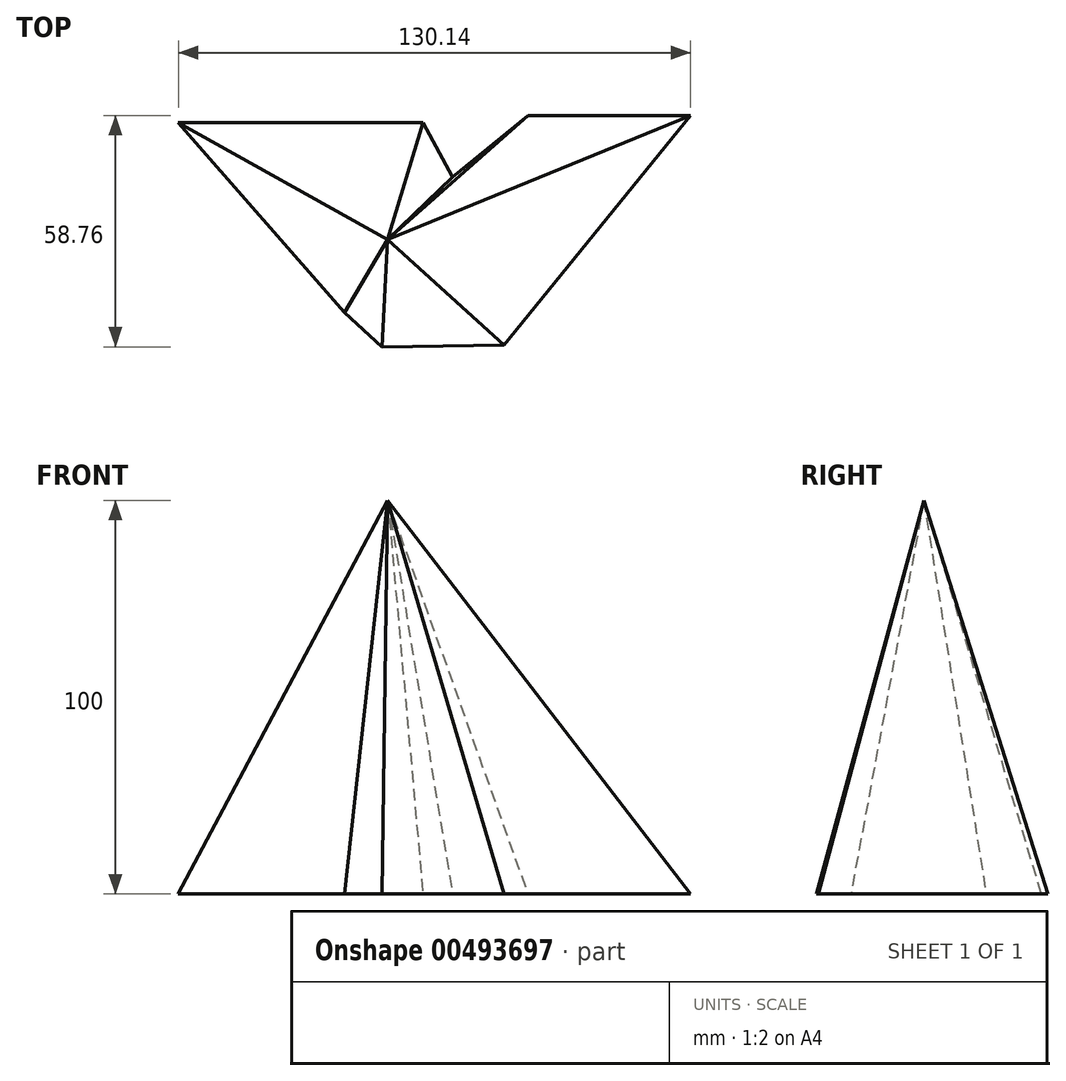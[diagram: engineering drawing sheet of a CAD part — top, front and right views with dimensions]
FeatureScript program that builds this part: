
annotation { "Feature Type Name" : "Feature", "Feature Type Description" : "" }
export const myFeature = defineFeature(function(context is Context, id is Id, definition is map)
    precondition{}
    {
        {
            var Q0;
            Q0=qCreatedBy(makeId("Top.planeOp"),FACE);
            var sketch = newSketch(context, id + "F0", { "sketchPlane" : qUnion([Q0])});
            skLineSegment(sketch, "E0", {"start": v(-62.14, 38.45) * mm, "end": v(0, 38.45) * mm});
            skLineSegment(sketch, "E1", {"start": v(0, 38.45) * mm, "end": v(7.5, 24.52) * mm});
            skLineSegment(sketch, "E2", {"start": v(7.5, 24.52) * mm, "end": v(26.65, 40.19) * mm});
            skLineSegment(sketch, "E3", {"start": v(26.65, 40.19) * mm, "end": v(68, 40.19) * mm});
            skLineSegment(sketch, "E4", {"start": v(-62.14, 38.45) * mm, "end": v(-19.92, -9.87) * mm});
            skLineSegment(sketch, "E5", {"start": v(68, 40.19) * mm, "end": v(20.55, -18.14) * mm});
            skLineSegment(sketch, "E6", {"start": v(-19.92, -9.87) * mm, "end": v(-10.35, -18.57) * mm});
            skLineSegment(sketch, "E7", {"start": v(-10.35, -18.57) * mm, "end": v(20.55, -18.14) * mm});
            skSolve(sketch);
        }
        {
            var Q0;
            Q0=qCreatedBy(makeId("Top.planeOp"),FACE);
            cPlane(context, id + "F1", {"entities" : qUnion([Q0]), "cplaneType" : CPlaneType.OFFSET, "offset" : 100 * mm, "width" : 150 * mm, "height" : 150 * mm});
        }
        {
            var Q0;
            Q0=qCreatedBy(id+"F1.planeOp",FACE);
            var sketch = newSketch(context, id + "F2", { "sketchPlane" : qUnion([Q0])});
            skPoint(sketch, "E8", {"position": v(-8.97, 8.67) * mm});
            skSolve(sketch);
        }
        {
            var Q0;
            Q0=sQuery(id+"F2.wireOp",VERTEX,"E8");
            var Q1;
            Q1=makeQuery(id+"F0.imprint","IMPRINT",FACE,{"disambiguationData":[TD([[makeQuery(id+"F0.imprint","IMPRINT",EDGE,{"derivedFrom":sQuery(id+"F0.wireOp",EDGE,"E0")}),-1.0]])]});
            loft(context, id + "F3", {"sheetProfilesArray" : [{ "sheetProfileEntities" : qUnion([Q0]) }, { "sheetProfileEntities" : qUnion([Q1]) }]});
        }
    });
